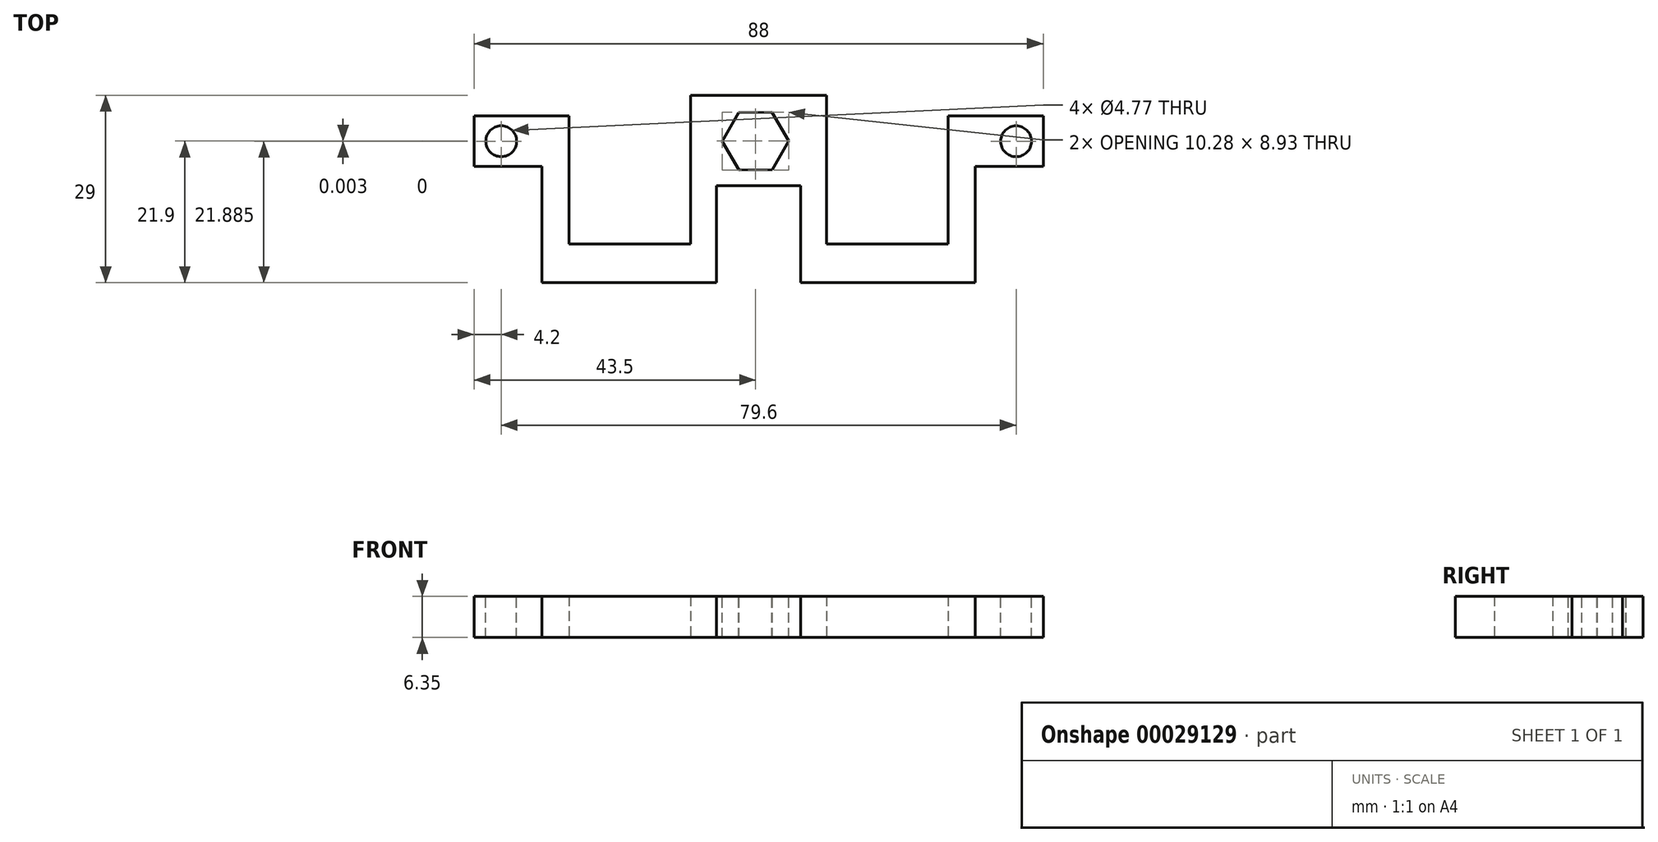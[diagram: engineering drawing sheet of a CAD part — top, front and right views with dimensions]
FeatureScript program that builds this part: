
annotation { "Feature Type Name" : "Feature", "Feature Type Description" : "" }
export const myFeature = defineFeature(function(context is Context, id is Id, definition is map)
    precondition{}
    {
        {
            var Q0;
            Q0=qCreatedBy(makeId("Top.planeOp"),FACE);
            var sketch = newSketch(context, id + "F0", { "sketchPlane" : qUnion([Q0])});
            skLineSegment(sketch, "E0", {"start": v(0, 0) * mm, "end": v(0, 18) * mm});
            skLineSegment(sketch, "E1", {"start": v(0, 18) * mm, "end": v(10.5, 18) * mm});
            skLineSegment(sketch, "E2", {"start": v(10.5, 18) * mm, "end": v(10.5, 25.8) * mm});
            skLineSegment(sketch, "E3", {"start": v(10.5, 25.8) * mm, "end": v(-4.2, 25.8) * mm});
            skLineSegment(sketch, "E4", {"start": v(-4.2, 25.8) * mm, "end": v(-4.2, 6) * mm});
            skLineSegment(sketch, "E5", {"start": v(-4.2, 6) * mm, "end": v(-23, 6) * mm});
            skLineSegment(sketch, "E6", {"start": v(-23, 6) * mm, "end": v(-23, 29) * mm});
            skLineSegment(sketch, "E7", {"start": v(-40, 15) * mm, "end": v(-27, 15) * mm});
            skLineSegment(sketch, "E8", {"start": v(-27, 15) * mm, "end": v(-27, 0) * mm});
            skLineSegment(sketch, "E9", {"start": v(-27, 0) * mm, "end": v(0, 0) * mm});
            skLineSegment(sketch, "E10", {"start": v(-40, 15) * mm, "end": v(-40, 0) * mm});
            skLineSegment(sketch, "E11", {"start": v(-40, 0) * mm, "end": v(-67, 0) * mm});
            skLineSegment(sketch, "E12", {"start": v(-67, 0) * mm, "end": v(-67, 18) * mm});
            skLineSegment(sketch, "E13", {"start": v(-67, 18) * mm, "end": v(-77.5, 18) * mm});
            skLineSegment(sketch, "E14", {"start": v(-77.5, 18) * mm, "end": v(-77.5, 25.8) * mm});
            skLineSegment(sketch, "E15", {"start": v(-77.5, 25.8) * mm, "end": v(-62.8, 25.8) * mm});
            skLineSegment(sketch, "E16", {"start": v(-62.8, 25.8) * mm, "end": v(-62.8, 6) * mm});
            skLineSegment(sketch, "E17", {"start": v(-62.8, 6) * mm, "end": v(-44, 6) * mm});
            skLineSegment(sketch, "E18", {"start": v(-44, 6) * mm, "end": v(-44, 29) * mm});
            skLineSegment(sketch, "E19", {"start": v(-44, 29) * mm, "end": v(-23, 29) * mm});
            skSolve(sketch);
        }
        {
            var Q0;
            Q0=qSketchRegion(id+"F0",true);
            extrude(context, id + "F1", {"entities" : qUnion([Q0]), "depth" : 6.35 * mm});
        }
        {
            var Q0;
            Q0=makeQuery(id+"F1.opExtrude","CAP_FACE",FACE,{"disambiguationData":[OSD([sQuery(id+"F0.wireOp",EDGE,"E0"),sQuery(id+"F0.wireOp",EDGE,"E1"),sQuery(id+"F0.wireOp",EDGE,"E2"),sQuery(id+"F0.wireOp",EDGE,"E3"),sQuery(id+"F0.wireOp",EDGE,"E4"),sQuery(id+"F0.wireOp",EDGE,"E5"),sQuery(id+"F0.wireOp",EDGE,"E6"),sQuery(id+"F0.wireOp",EDGE,"bc51e97a-136a-48b4-80d2-e410240dacd7"),sQuery(id+"F0.wireOp",EDGE,"0d0877c4-4f41-446d-b3a6-0541d20c0740"),sQuery(id+"F0.wireOp",EDGE,"E7"),sQuery(id+"F0.wireOp",EDGE,"E8"),sQuery(id+"F0.wireOp",EDGE,"E9")])],"isStart":false});
            var sketch = newSketch(context, id + "F2", { "sketchPlane" : qUnion([Q0])});
            skCircle(sketch, "E20", {"center": v(6.3, 21.89) * mm, "radius": 2.38 * mm});
            skCircle(sketch, "E21", {"center": v(-34, 21.9) * mm, "radius": 4.45 * mm});
            skCircle(sketch, "E22.cCircle", {"center": v(6.3, 21.89) * mm, "radius": 2.38 * mm, "construction": true});
            skPoint(sketch, "E22.0.midPoint", {"position": v(3.92, 21.89) * mm});
            skCircle(sketch, "E23", {"center": v(-73.3, 21.89) * mm, "radius": 2.38 * mm});
            skCircle(sketch, "E24.cCircle", {"center": v(-34, 21.9) * mm, "radius": 4.45 * mm, "construction": true});
            skLineSegment(sketch, "E24.0", {"start": v(-31.46, 26.37) * mm, "end": v(-28.86, 21.93) * mm});
            skLineSegment(sketch, "E24.1", {"start": v(-28.86, 21.93) * mm, "end": v(-31.4, 17.47) * mm});
            skLineSegment(sketch, "E24.2", {"start": v(-31.4, 17.47) * mm, "end": v(-36.54, 17.43) * mm});
            skLineSegment(sketch, "E24.3", {"start": v(-36.54, 17.43) * mm, "end": v(-39.14, 21.87) * mm});
            skLineSegment(sketch, "E24.4", {"start": v(-39.14, 21.87) * mm, "end": v(-36.6, 26.33) * mm});
            skLineSegment(sketch, "E24.5", {"start": v(-36.6, 26.33) * mm, "end": v(-31.46, 26.37) * mm});
            skPoint(sketch, "E24.0.midPoint", {"position": v(-30.16, 24.15) * mm});
            skSolve(sketch);
        }
        {
            var Q0;
            {var subQ0=sQuery(id+"F2.wireOp",EDGE,"E21");var subQ6=makeQuery(id+"F2.imprint","INTERSECT",VERTEX,{"derivedFrom":[subQ0,sQuery(id+"F2.wireOp",EDGE,"b22fa30f-7d92-411e-b9dc-695adf4c461f.5")]});Q0=makeQuery(id+"F2.imprint","IMPRINT",FACE,{"disambiguationData":[TD([[makeQuery(id+"F2.imprint","IMPRINT",EDGE,{"disambiguationData":[TD([[subQ6,1.0]])],"derivedFrom":subQ0}),1.0]])]});}
            var Q1;
            {var subQ0=sQuery(id+"F2.wireOp",EDGE,"E20");var subQ6=makeQuery(id+"F2.imprint","INTERSECT",VERTEX,{"derivedFrom":[subQ0,sQuery(id+"F2.wireOp",EDGE,"E22.2")]});Q1=makeQuery(id+"F2.imprint","IMPRINT",FACE,{"disambiguationData":[TD([[makeQuery(id+"F2.imprint","IMPRINT",EDGE,{"disambiguationData":[TD([[subQ6,1.0]])],"derivedFrom":subQ0}),1.0]])]});}
            var Q2;
            {var subQ0=sQuery(id+"F2.wireOp",EDGE,"b22fa30f-7d92-411e-b9dc-695adf4c461f.5");var subQ1=sQuery(id+"F2.wireOp",EDGE,"E21");var subQ2=makeQuery(id+"F2.imprint","INTERSECT",VERTEX,{"derivedFrom":[subQ1,subQ0]});Q2=makeQuery(id+"F2.imprint","IMPRINT",FACE,{"disambiguationData":[TD([[makeQuery(id+"F2.imprint","IMPRINT",EDGE,{"disambiguationData":[TD([[subQ2,-1.0]])],"derivedFrom":subQ1}),-1.0]])]});}
            var Q3;
            {var subQ0=sQuery(id+"F2.wireOp",EDGE,"b22fa30f-7d92-411e-b9dc-695adf4c461f.5");var subQ1=sQuery(id+"F2.wireOp",EDGE,"E21");var subQ2=makeQuery(id+"F2.imprint","INTERSECT",VERTEX,{"derivedFrom":[subQ1,subQ0]});Q3=makeQuery(id+"F2.imprint","IMPRINT",FACE,{"disambiguationData":[TD([[makeQuery(id+"F2.imprint","IMPRINT",EDGE,{"disambiguationData":[TD([[subQ2,1.0]])],"derivedFrom":subQ1}),-1.0]])]});}
            var Q4;
            {var subQ1=sQuery(id+"F2.wireOp",EDGE,"E21");var subQ3=sQuery(id+"F2.wireOp",EDGE,"b22fa30f-7d92-411e-b9dc-695adf4c461f.0");var subQ5=makeQuery(id+"F2.imprint","INTERSECT",VERTEX,{"derivedFrom":[subQ1,subQ3]});Q4=makeQuery(id+"F2.imprint","IMPRINT",FACE,{"disambiguationData":[TD([[makeQuery(id+"F2.imprint","IMPRINT",EDGE,{"disambiguationData":[TD([[subQ5,1.0]])],"derivedFrom":subQ1}),-1.0]])]});}
            var Q5;
            {var subQ0=sQuery(id+"F2.wireOp",EDGE,"b22fa30f-7d92-411e-b9dc-695adf4c461f.2");var subQ1=sQuery(id+"F2.wireOp",EDGE,"E21");var subQ2=makeQuery(id+"F2.imprint","INTERSECT",VERTEX,{"derivedFrom":[subQ1,subQ0]});Q5=makeQuery(id+"F2.imprint","IMPRINT",FACE,{"disambiguationData":[TD([[makeQuery(id+"F2.imprint","IMPRINT",EDGE,{"disambiguationData":[TD([[subQ2,-1.0]])],"derivedFrom":subQ1}),-1.0]])]});}
            var Q6;
            Q6=makeQuery(id+"F2.imprint","IMPRINT",FACE,{"disambiguationData":[TD([[makeQuery(id+"F2.imprint","IMPRINT",EDGE,{"derivedFrom":sQuery(id+"F2.wireOp",EDGE,"E20")}),1.0]])]});
            var Q7;
            {var subQ0=sQuery(id+"F2.wireOp",EDGE,"b22fa30f-7d92-411e-b9dc-695adf4c461f.4");var subQ1=sQuery(id+"F2.wireOp",EDGE,"E21");var subQ2=makeQuery(id+"F2.imprint","INTERSECT",VERTEX,{"derivedFrom":[subQ1,subQ0]});Q7=makeQuery(id+"F2.imprint","IMPRINT",FACE,{"disambiguationData":[TD([[makeQuery(id+"F2.imprint","IMPRINT",EDGE,{"disambiguationData":[TD([[subQ2,-1.0]])],"derivedFrom":subQ1}),-1.0]])]});}
            var Q8;
            {var subQ0=sQuery(id+"F2.wireOp",EDGE,"b22fa30f-7d92-411e-b9dc-695adf4c461f.3");var subQ1=sQuery(id+"F2.wireOp",EDGE,"E21");var subQ2=makeQuery(id+"F2.imprint","INTERSECT",VERTEX,{"derivedFrom":[subQ1,subQ0]});Q8=makeQuery(id+"F2.imprint","IMPRINT",FACE,{"disambiguationData":[TD([[makeQuery(id+"F2.imprint","IMPRINT",EDGE,{"disambiguationData":[TD([[subQ2,-1.0]])],"derivedFrom":subQ1}),-1.0]])]});}
            var Q9;
            Q9=makeQuery(id+"F2.imprint","IMPRINT",FACE,{"disambiguationData":[TD([[makeQuery(id+"F2.imprint","IMPRINT",EDGE,{"derivedFrom":sQuery(id+"F2.wireOp",EDGE,"E23")}),1.0]])]});
            extrude(context, id + "F3", {"entities" : qUnion([Q0, Q1, Q2, Q3, Q4, Q5, Q6, Q7, Q8, Q9]), "operationType" : NewBodyOperationType.REMOVE, "oppositeDirection" : true, "depth" : 6.35 * mm});
        }
    });
